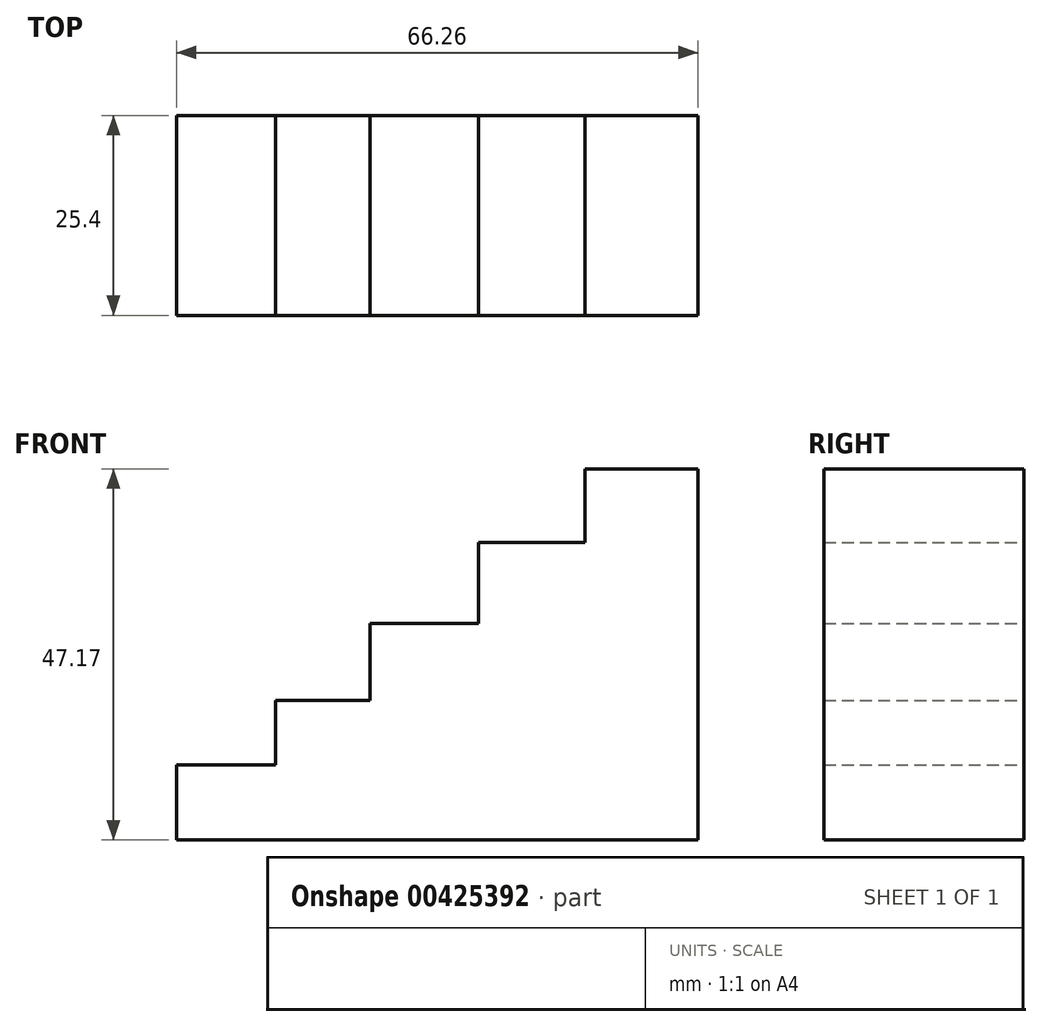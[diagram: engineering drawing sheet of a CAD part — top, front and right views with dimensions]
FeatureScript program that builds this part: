
annotation { "Feature Type Name" : "Feature", "Feature Type Description" : "" }
export const myFeature = defineFeature(function(context is Context, id is Id, definition is map)
    precondition{}
    {
        {
            var Q0;
            Q0=qCreatedBy(makeId("Front.planeOp"),FACE);
            var sketch = newSketch(context, id + "F0", { "sketchPlane" : qUnion([Q0])});
            skLineSegment(sketch, "E0", {"start": v(0, 0) * mm, "end": v(0, 47.17) * mm});
            skLineSegment(sketch, "E1", {"start": v(0, 47.17) * mm, "end": v(-14.32, 47.17) * mm});
            skLineSegment(sketch, "E2", {"start": v(-14.32, 47.17) * mm, "end": v(-14.32, 37.8) * mm});
            skLineSegment(sketch, "E3", {"start": v(-14.32, 37.8) * mm, "end": v(-27.88, 37.8) * mm});
            skLineSegment(sketch, "E4", {"start": v(-27.88, 37.8) * mm, "end": v(-27.88, 27.5) * mm});
            skLineSegment(sketch, "E5", {"start": v(-27.88, 27.5) * mm, "end": v(-41.63, 27.5) * mm});
            skLineSegment(sketch, "E6", {"start": v(-41.63, 27.5) * mm, "end": v(-41.63, 17.76) * mm});
            skLineSegment(sketch, "E7", {"start": v(-41.63, 17.76) * mm, "end": v(-53.66, 17.76) * mm});
            skLineSegment(sketch, "E8", {"start": v(-53.66, 17.76) * mm, "end": v(-53.66, 9.55) * mm});
            skLineSegment(sketch, "E9", {"start": v(-53.66, 9.55) * mm, "end": v(-66.26, 9.55) * mm});
            skLineSegment(sketch, "E10", {"start": v(-66.26, 9.55) * mm, "end": v(-66.26, 0) * mm});
            skLineSegment(sketch, "E11", {"start": v(-66.26, 0) * mm, "end": v(0, 0) * mm});
            skSolve(sketch);
        }
        {
            var Q0;
            Q0=makeQuery(id+"F0.imprint","IMPRINT",FACE,{"disambiguationData":[TD([[makeQuery(id+"F0.imprint","IMPRINT",EDGE,{"derivedFrom":sQuery(id+"F0.wireOp",EDGE,"E0")}),1.0]])]});
            extrude(context, id + "F1", {"entities" : qUnion([Q0]), "depth" : 25.4 * mm});
        }
    });
